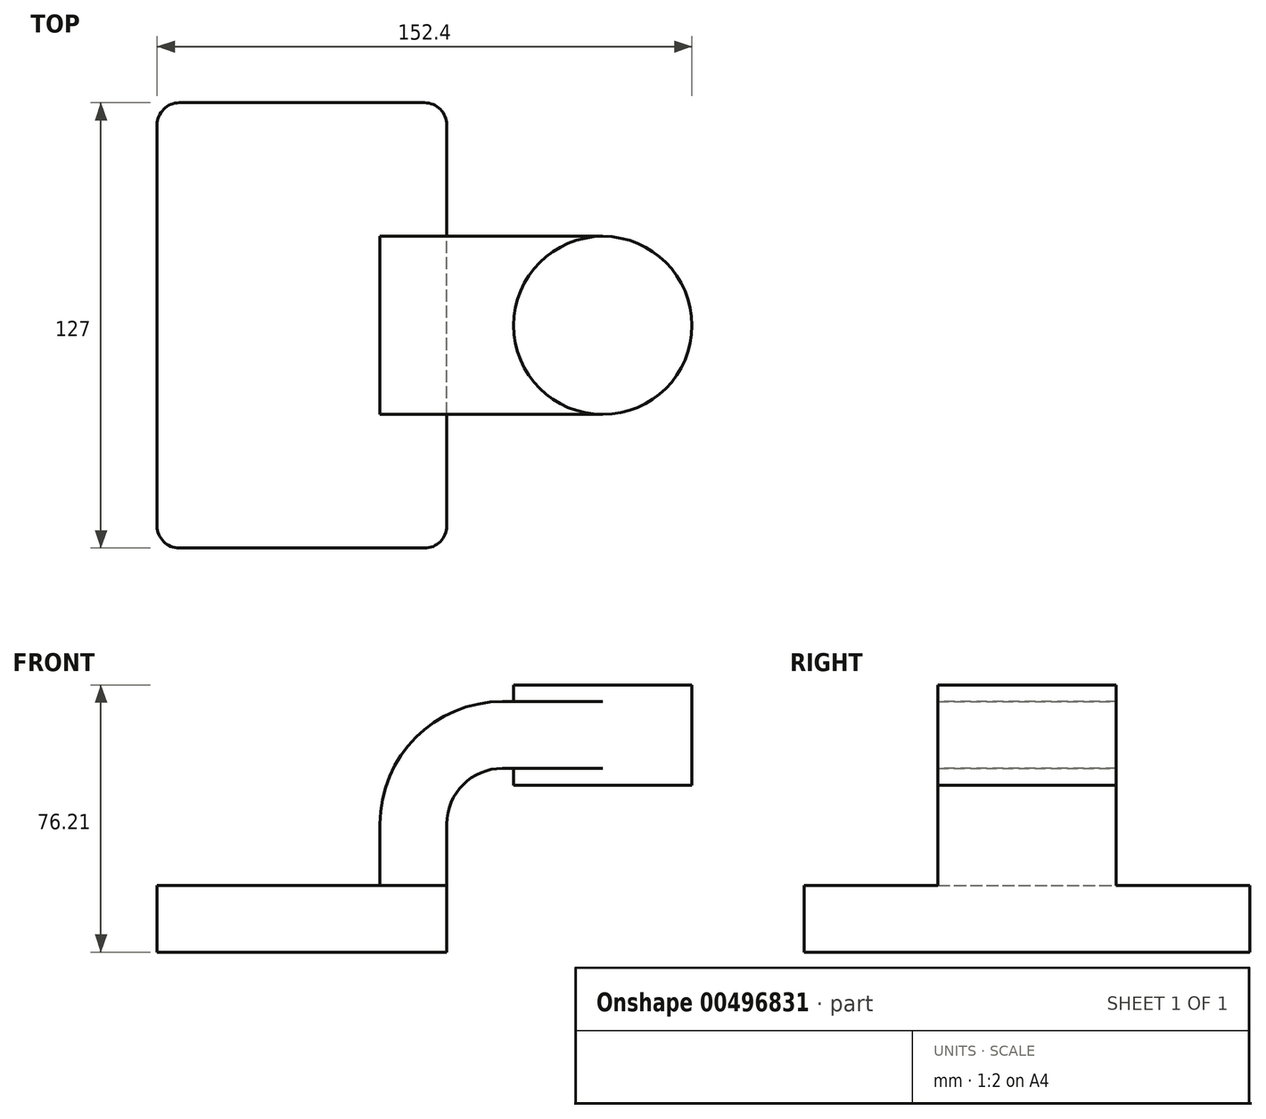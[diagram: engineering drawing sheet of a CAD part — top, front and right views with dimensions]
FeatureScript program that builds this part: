
annotation { "Feature Type Name" : "Feature", "Feature Type Description" : "" }
export const myFeature = defineFeature(function(context is Context, id is Id, definition is map)
    precondition{}
    {
        {
            var Q0;
            Q0=qCreatedBy(makeId("Front.planeOp"),FACE);
            var sketch = newSketch(context, id + "F0", { "sketchPlane" : qUnion([Q0])});
            skLineSegment(sketch, "E0.bottom", {"start": v(41.27, 9.53) * mm, "end": v(-41.28, 9.53) * mm});
            skLineSegment(sketch, "E0.top", {"start": v(41.28, -9.52) * mm, "end": v(-41.27, -9.52) * mm});
            skLineSegment(sketch, "E0.left", {"start": v(41.28, 9.53) * mm, "end": v(41.28, -9.52) * mm});
            skLineSegment(sketch, "E0.right", {"start": v(-41.28, 9.53) * mm, "end": v(-41.27, -9.52) * mm});
            skPoint(sketch, "E0.middle", {"position": v(0, 0) * mm});
            skLineSegment(sketch, "E1.bottom", {"start": v(111.12, 66.68) * mm, "end": v(60.33, 66.68) * mm});
            skLineSegment(sketch, "E1.top", {"start": v(111.12, 38.1) * mm, "end": v(60.33, 38.1) * mm});
            skLineSegment(sketch, "E1.left", {"start": v(111.12, 66.67) * mm, "end": v(111.12, 38.1) * mm});
            skLineSegment(sketch, "E1.right", {"start": v(60.32, 66.67) * mm, "end": v(60.33, 38.1) * mm});
            skPoint(sketch, "E1.middle", {"position": v(85.72, 52.39) * mm});
            skLineSegment(sketch, "E2", {"start": v(41.27, 9.53) * mm, "end": v(41.27, 27) * mm});
            skArc(sketch, "E3", {"start": v(41.27, 27) * mm, "mid": v(45.92, 38.23) * mm, "end": v(57.15, 42.88) * mm});
            skLineSegment(sketch, "E4", {"start": v(57.15, 42.88) * mm, "end": v(85.73, 42.88) * mm});
            skLineSegment(sketch, "E5.0", {"start": v(57.15, 61.93) * mm, "end": v(85.72, 61.93) * mm});
            skArc(sketch, "E5.1", {"start": v(22.23, 27) * mm, "mid": v(32.45, 51.7) * mm, "end": v(57.15, 61.93) * mm});
            skLineSegment(sketch, "E5.2", {"start": v(22.22, 9.53) * mm, "end": v(22.22, 27) * mm});
            skFitSpline(sketch, "E6", {"points": [v(-41.28, 9.52) * mm, v(57.15, 61.93) * mm], "startDerivative": vector(1.25, 108.9) * mm, "endDerivative": vector(141.53, -19.47) * mm});
            skPoint(sketch, "E7", {"position": v(85.72, 66.68) * mm});
            skLineSegment(sketch, "E8", {"start": v(85.72, 66.68) * mm, "end": v(85.72, 38.1) * mm});
            skSolve(sketch);
        }
        {
            var Q0;
            Q0=makeQuery(id+"F0.imprint","IMPRINT",FACE,{"disambiguationData":[TD([[makeQuery(id+"F0.imprint","IMPRINT",EDGE,{"derivedFrom":sQuery(id+"F0.wireOp",EDGE,"E0.top")}),-1.0]])]});
            extrude(context, id + "F1", {"entities" : qUnion([Q0]), "endBound" : BoundingType.SYMMETRIC, "depth" : 127 * mm});
        }
        {
            var Q0;
            {var subQ1=sQuery(id+"F0.wireOp",EDGE,"E2");Q0=makeQuery(id+"F0.imprint","IMPRINT",FACE,{"disambiguationData":[TD([[makeQuery(id+"F0.imprint","IMPRINT",EDGE,{"derivedFrom":subQ1}),1.0]])]});}
            var Q1;
            {var subQ0=sQuery(id+"F0.wireOp",EDGE,"E5.0");var subQ1=sQuery(id+"F0.wireOp",EDGE,"E1.right");var subQ2=makeQuery(id+"F0.imprint","INTERSECT",VERTEX,{"derivedFrom":[subQ1,subQ0]});Q1=makeQuery(id+"F0.imprint","IMPRINT",FACE,{"disambiguationData":[TD([[makeQuery(id+"F0.imprint","IMPRINT",EDGE,{"disambiguationData":[TD([[subQ2,-1.0]])],"derivedFrom":subQ1}),1.0]])]});}
            extrude(context, id + "F2", {"entities" : qUnion([Q0, Q1]), "operationType" : NewBodyOperationType.ADD, "endBound" : BoundingType.SYMMETRIC, "depth" : 50.8 * mm});
        }
        {
            var Q0;
            Q0=makeQuery(id+"F0.imprint","IMPRINT",FACE,{"disambiguationData":[TD([[makeQuery(id+"F0.imprint","IMPRINT",EDGE,{"derivedFrom":sQuery(id+"F0.wireOp",EDGE,"E5.1")}),1.0]])]});
            extrude(context, id + "F3", {"entities" : qUnion([Q0]), "operationType" : NewBodyOperationType.ADD, "endBound" : BoundingType.SYMMETRIC, "depth" : 15.88 * mm});
        }
        {
            var Q0;
            {var subQ0=sQuery(id+"F0.wireOp",EDGE,"E1.left");Q0=makeQuery(id+"F0.imprint","IMPRINT",FACE,{"disambiguationData":[TD([[makeQuery(id+"F0.imprint","IMPRINT",EDGE,{"derivedFrom":subQ0}),-1.0]])]});}
            var Q1;
            Q1=sQuery(id+"F0.wireOp",EDGE,"E8");
            revolve(context, id + "F4", {"operationType" : NewBodyOperationType.ADD, "entities" : qUnion([Q0]), "axis" : qUnion([Q1]), "revolveType" : RevolveType.FULL});
        }
        {
            var Q0;
            Q0=makeQuery(id+"F1.opExtrude","CAP_EDGE",EDGE,{"disambiguationData":[OSD([sQuery(id+"F0.wireOp",EDGE,"E0.right")])],"isStart":false});
            var Q1;
            Q1=makeQuery(id+"F1.opExtrude","CAP_EDGE",EDGE,{"disambiguationData":[OSD([sQuery(id+"F0.wireOp",EDGE,"E0.left")])],"isStart":false});
            var Q2;
            Q2=makeQuery(id+"F1.opExtrude","CAP_EDGE",EDGE,{"disambiguationData":[OSD([sQuery(id+"F0.wireOp",EDGE,"E0.left")])],"isStart":true});
            var Q3;
            Q3=makeQuery(id+"F1.opExtrude","CAP_EDGE",EDGE,{"disambiguationData":[OSD([sQuery(id+"F0.wireOp",EDGE,"E0.right")])],"isStart":true});
            fillet(context, id + "F5", {"entities" : qUnion([Q0, Q1, Q2, Q3]), "radius" : 6.35 * mm, "tangentPropagation" : true, "allowEdgeOverflow" : false});
        }
    });
